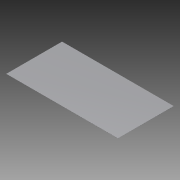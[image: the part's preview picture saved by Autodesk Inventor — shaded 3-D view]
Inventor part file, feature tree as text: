
AUTODESK INVENTOR PART (.ipt)
format: ipt  version: 2012 (Build 160160000, 160)  size: 67,072 bytes
history: native  units: in
note: dims shown in document units (in); Inventor stores cm internally (conversion verified against a paired STEP export)
features: extrude x1, sketch x1
ambient origin geometry x8: Origin, YZ Plane, XZ Plane, XY Plane, X Axis, Y Axis, Z Axis, Center Point
bodies: Solid1 (feature_tree)
feature tree (2):
  extrude  "Extrusion1"  Depth=648.0in
  sketch  "Sketch1"  dims[d0=0.5in d1=648.0in d2=324.0in d3=0.0in]
